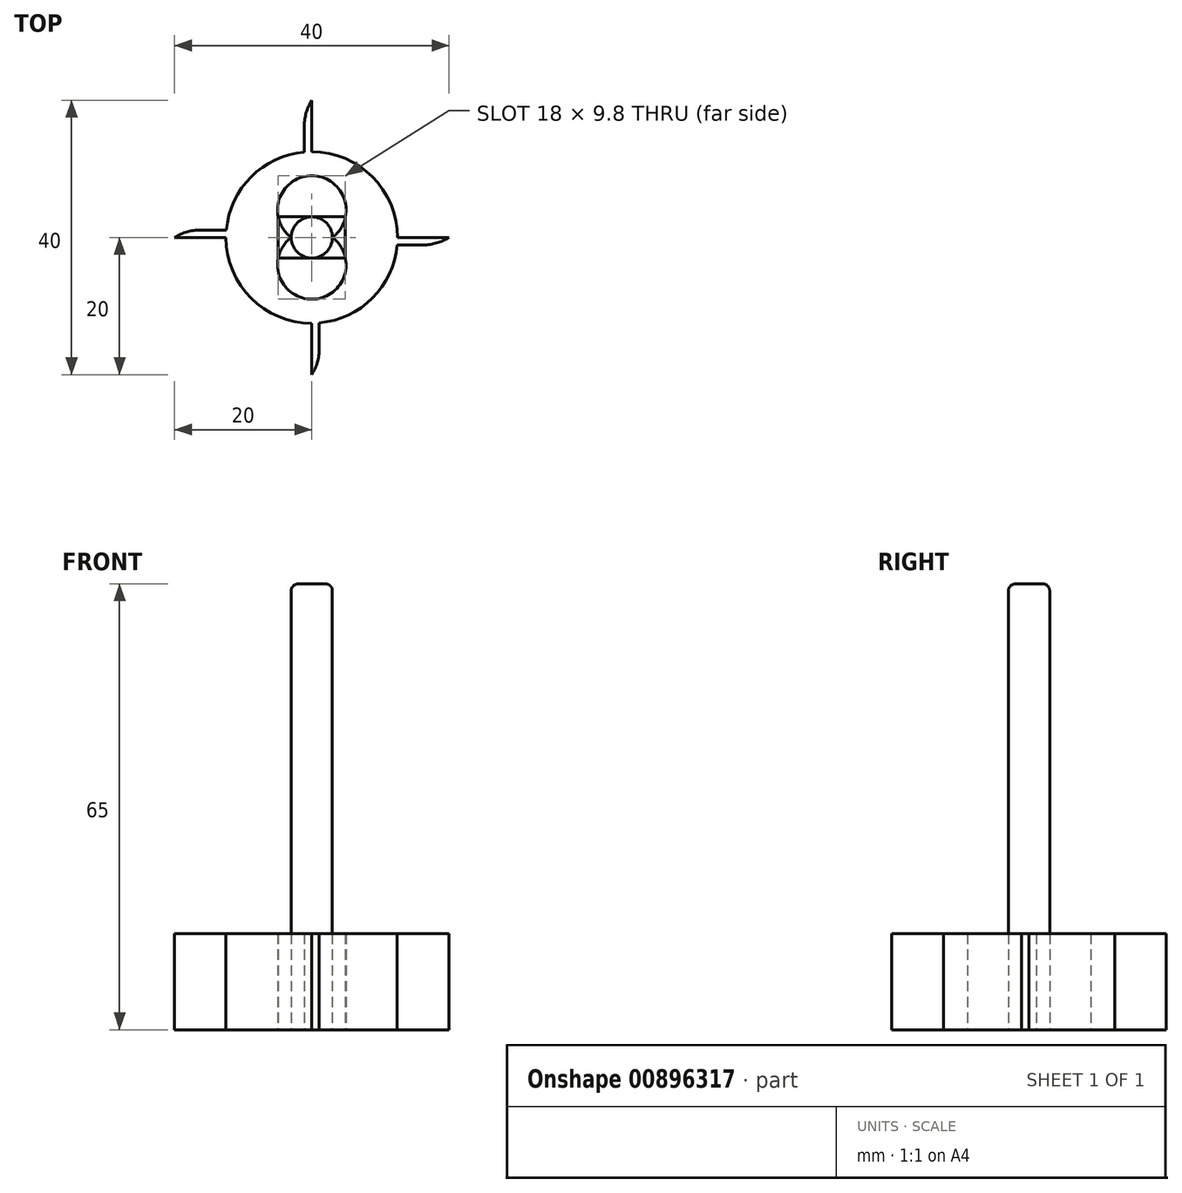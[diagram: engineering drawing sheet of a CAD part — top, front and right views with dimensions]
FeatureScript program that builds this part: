
annotation { "Feature Type Name" : "Feature", "Feature Type Description" : "" }
export const myFeature = defineFeature(function(context is Context, id is Id, definition is map)
    precondition{}
    {
        {
            var Q0;
            Q0=qCreatedBy(makeId("Top.planeOp"),FACE);
            var sketch = newSketch(context, id + "F0", { "sketchPlane" : qUnion([Q0])});
            skCircle(sketch, "E0", {"center": v(0, 0) * mm, "radius": 3 * mm});
            skCircle(sketch, "E1", {"center": v(0, 0) * mm, "radius": 12.5 * mm});
            skLineSegment(sketch, "E2", {"start": v(0, 0) * mm, "end": v(20, 0) * mm});
            skLineSegment(sketch, "E3", {"start": v(0, 0) * mm, "end": v(-20, 0) * mm});
            skArc(sketch, "E4", {"start": v(12.5, 0) * mm, "mid": v(16.25, -1.09) * mm, "end": v(20, 0) * mm});
            skLineSegment(sketch, "E5", {"start": v(0, 0) * mm, "end": v(0, -20) * mm});
            skLineSegment(sketch, "E6", {"start": v(0, -20) * mm, "end": v(0, 20) * mm});
            skLineSegment(sketch, "E7.MirrorCS", {"start": v(0, 20) * mm, "end": v(0, -20) * mm});
            skArc(sketch, "E8", {"start": v(0, -20) * mm, "mid": v(1.09, -16.25) * mm, "end": v(0, -12.5) * mm});
            skArc(sketch, "E9", {"start": v(-12.5, 0) * mm, "mid": v(-16.25, 1.09) * mm, "end": v(-20, 0) * mm});
            skArc(sketch, "E10", {"start": v(0, 20) * mm, "mid": v(-1.09, 16.25) * mm, "end": v(0, 12.5) * mm});
            skLineSegment(sketch, "E11", {"start": v(1.09, -16.25) * mm, "end": v(1.09, -12.45) * mm});
            skLineSegment(sketch, "E12", {"start": v(-16.25, 1.09) * mm, "end": v(-12.45, 1.09) * mm});
            skLineSegment(sketch, "E13", {"start": v(-1.09, 16.25) * mm, "end": v(-1.09, 12.45) * mm});
            skLineSegment(sketch, "E14", {"start": v(16.25, -1.09) * mm, "end": v(12.45, -1.09) * mm});
            skArc(sketch, "E15", {"start": v(-3, 0) * mm, "mid": v(0, -9) * mm, "end": v(3, 0) * mm});
            skArc(sketch, "E16", {"start": v(3, 0) * mm, "mid": v(0, 9) * mm, "end": v(-3, 0) * mm});
            skLineSegment(sketch, "E17", {"start": v(0, 3) * mm, "end": v(-4.9, 3) * mm});
            skLineSegment(sketch, "E18", {"start": v(-4.9, 3) * mm, "end": v(4.9, 3) * mm});
            skLineSegment(sketch, "E19", {"start": v(0, -3) * mm, "end": v(-4.9, -3) * mm});
            skLineSegment(sketch, "E20", {"start": v(-4.9, -3) * mm, "end": v(4.9, -3) * mm});
            skLineSegment(sketch, "E21", {"start": v(4.9, 3) * mm, "end": v(4.9, -3) * mm});
            skLineSegment(sketch, "E22", {"start": v(-4.9, 3) * mm, "end": v(-4.9, -3) * mm});
            skSolve(sketch);
        }
        {
            var Q0;
            {var subQ0=sQuery(id+"F0.wireOp",EDGE,"E5");var subQ1=sQuery(id+"F0.wireOp",EDGE,"E0");var subQ2=makeQuery(id+"F0.imprint","INTERSECT",VERTEX,{"derivedFrom":[subQ1,subQ0,sQuery(id+"F0.wireOp",EDGE,"E19"),sQuery(id+"F0.wireOp",EDGE,"E20")]});Q0=makeQuery(id+"F0.imprint","IMPRINT",FACE,{"disambiguationData":[TD([[makeQuery(id+"F0.imprint","IMPRINT",EDGE,{"disambiguationData":[TD([[subQ2,-1.0]])],"derivedFrom":subQ1}),1.0]])]});}
            var Q1;
            {var subQ0=sQuery(id+"F0.wireOp",EDGE,"E6");var subQ1=sQuery(id+"F0.wireOp",EDGE,"E0");var subQ2=makeQuery(id+"F0.imprint","INTERSECT",VERTEX,{"derivedFrom":[subQ1,subQ0,sQuery(id+"F0.wireOp",EDGE,"E17"),sQuery(id+"F0.wireOp",EDGE,"E18")]});Q1=makeQuery(id+"F0.imprint","IMPRINT",FACE,{"disambiguationData":[TD([[makeQuery(id+"F0.imprint","IMPRINT",EDGE,{"disambiguationData":[TD([[subQ2,1.0]])],"derivedFrom":subQ1}),1.0]])]});}
            var Q2;
            {var subQ0=sQuery(id+"F0.wireOp",EDGE,"E5");var subQ1=sQuery(id+"F0.wireOp",EDGE,"E0");var subQ2=makeQuery(id+"F0.imprint","INTERSECT",VERTEX,{"derivedFrom":[subQ1,subQ0,sQuery(id+"F0.wireOp",EDGE,"E19"),sQuery(id+"F0.wireOp",EDGE,"E20")]});var subQ7=sQuery(id+"F0.wireOp",EDGE,"E6");var subQ10=makeQuery(id+"F0.imprint","INTERSECT",VERTEX,{"derivedFrom":[subQ1,subQ7,sQuery(id+"F0.wireOp",EDGE,"E17"),sQuery(id+"F0.wireOp",EDGE,"E18")]});Q2=qUnion([makeQuery(id+"F0.imprint","IMPRINT",FACE,{"disambiguationData":[TD([[makeQuery(id+"F0.imprint","IMPRINT",EDGE,{"disambiguationData":[TD([[subQ10,-1.0]])],"derivedFrom":subQ1}),1.0]])]}),makeQuery(id+"F0.imprint","IMPRINT",FACE,{"disambiguationData":[TD([[makeQuery(id+"F0.imprint","IMPRINT",EDGE,{"disambiguationData":[TD([[subQ2,-1.0]])],"derivedFrom":subQ1}),1.0]])]})]);}
            var Q3;
            {var subQ0=sQuery(id+"F0.wireOp",EDGE,"E5");var subQ1=sQuery(id+"F0.wireOp",EDGE,"E0");var subQ2=makeQuery(id+"F0.imprint","INTERSECT",VERTEX,{"derivedFrom":[subQ1,subQ0,sQuery(id+"F0.wireOp",EDGE,"E19"),sQuery(id+"F0.wireOp",EDGE,"E20")]});Q3=makeQuery(id+"F0.imprint","IMPRINT",FACE,{"disambiguationData":[TD([[makeQuery(id+"F0.imprint","IMPRINT",EDGE,{"disambiguationData":[TD([[subQ2,1.0]])],"derivedFrom":subQ1}),1.0]])]});}
            extrude(context, id + "F1", {"entities" : qUnion([Q0, Q1, Q2, Q3]), "depth" : 65 * mm, "offsetDistance" : 25 * mm});
        }
        {
            var Q0;
            {var subQ1=sQuery(id+"F0.wireOp",EDGE,"E1");var subQ3=makeQuery(id+"F0.imprint","INTERSECT",VERTEX,{"derivedFrom":[subQ1,sQuery(id+"F0.wireOp",EDGE,"E12")]});Q0=makeQuery(id+"F0.imprint","IMPRINT",FACE,{"disambiguationData":[TD([[makeQuery(id+"F0.imprint","IMPRINT",EDGE,{"disambiguationData":[TD([[subQ3,1.0]])],"derivedFrom":subQ1}),1.0]])]});}
            var Q1;
            {var subQ0=sQuery(id+"F0.wireOp",EDGE,"E22");var subQ7=sQuery(id+"F0.wireOp",EDGE,"E3");var subQ8=makeQuery(id+"F0.imprint","INTERSECT",VERTEX,{"derivedFrom":[subQ7,subQ0]});Q1=makeQuery(id+"F0.imprint","IMPRINT",FACE,{"disambiguationData":[TD([[makeQuery(id+"F0.imprint","IMPRINT",EDGE,{"disambiguationData":[TD([[subQ8,-1.0]])],"derivedFrom":subQ7}),1.0]])]});}
            var Q2;
            {var subQ3=sQuery(id+"F0.wireOp",EDGE,"E1");var subQ6=makeQuery(id+"F0.imprint","INTERSECT",VERTEX,{"derivedFrom":[subQ3,sQuery(id+"F0.wireOp",EDGE,"E11")]});Q2=makeQuery(id+"F0.imprint","IMPRINT",FACE,{"disambiguationData":[TD([[makeQuery(id+"F0.imprint","IMPRINT",EDGE,{"disambiguationData":[TD([[subQ6,-1.0]])],"derivedFrom":subQ3}),1.0]])]});}
            var Q3;
            {var subQ5=sQuery(id+"F0.wireOp",EDGE,"E21");var subQ7=sQuery(id+"F0.wireOp",EDGE,"E2");var subQ8=makeQuery(id+"F0.imprint","INTERSECT",VERTEX,{"derivedFrom":[subQ7,subQ5]});Q3=makeQuery(id+"F0.imprint","IMPRINT",FACE,{"disambiguationData":[TD([[makeQuery(id+"F0.imprint","IMPRINT",EDGE,{"disambiguationData":[TD([[subQ8,-1.0]])],"derivedFrom":subQ7}),1.0]])]});}
            var Q4;
            {var subQ0=sQuery(id+"F0.wireOp",EDGE,"E17");Q4=makeQuery(id+"F0.imprint","IMPRINT",FACE,{"disambiguationData":[TD([[makeQuery(id+"F0.imprint","IMPRINT",EDGE,{"derivedFrom":subQ0}),1.0]])]});}
            var Q5;
            {var subQ0=sQuery(id+"F0.wireOp",EDGE,"E18");Q5=makeQuery(id+"F0.imprint","IMPRINT",FACE,{"disambiguationData":[TD([[makeQuery(id+"F0.imprint","IMPRINT",EDGE,{"derivedFrom":subQ0}),-1.0]])]});}
            var Q6;
            {var subQ0=sQuery(id+"F0.wireOp",EDGE,"E20");Q6=makeQuery(id+"F0.imprint","IMPRINT",FACE,{"disambiguationData":[TD([[makeQuery(id+"F0.imprint","IMPRINT",EDGE,{"derivedFrom":subQ0}),1.0]])]});}
            var Q7;
            {var subQ0=sQuery(id+"F0.wireOp",EDGE,"E19");Q7=makeQuery(id+"F0.imprint","IMPRINT",FACE,{"disambiguationData":[TD([[makeQuery(id+"F0.imprint","IMPRINT",EDGE,{"derivedFrom":subQ0}),-1.0]])]});}
            extrude(context, id + "F2", {"entities" : qUnion([Q0, Q1, Q2, Q3, Q4, Q5, Q6, Q7]), "operationType" : NewBodyOperationType.ADD, "depth" : 14 * mm, "offsetDistance" : 25 * mm});
        }
        {
            var Q0;
            {var subQ0=sQuery(id+"F0.wireOp",EDGE,"df6b5224-9f47-4030-86d7-f893336ae27f0.MirrorCS");Q0=makeQuery(id+"F0.imprint","IMPRINT",FACE,{"disambiguationData":[TD([[makeQuery(id+"F0.imprint","IMPRINT",EDGE,{"derivedFrom":subQ0}),1.0]])]});}
            var Q1;
            {var subQ0=sQuery(id+"F0.wireOp",EDGE,"E4");var subQ1=sQuery(id+"F0.wireOp",EDGE,"E2");var subQ3=makeQuery(id+"F0.imprint","INTERSECT",VERTEX,{"derivedFrom":[subQ1,subQ0]});Q1=makeQuery(id+"F0.imprint","IMPRINT",FACE,{"disambiguationData":[TD([[makeQuery(id+"F0.imprint","IMPRINT",EDGE,{"disambiguationData":[TD([[subQ3,1.0]])],"derivedFrom":subQ0}),1.0]])]});}
            var Q2;
            {var subQ0=sQuery(id+"F0.wireOp",EDGE,"HRuZR72R-Es62-5aXc-brnB-5MRJDPJZIia5");Q2=makeQuery(id+"F0.imprint","IMPRINT",FACE,{"disambiguationData":[TD([[makeQuery(id+"F0.imprint","IMPRINT",EDGE,{"derivedFrom":subQ0}),1.0]])]});}
            var Q3;
            {var subQ0=sQuery(id+"F0.wireOp",EDGE,"ade42b69-f09c-4982-8809-a60c7d5ba8530.MirrorCS");Q3=makeQuery(id+"F0.imprint","IMPRINT",FACE,{"disambiguationData":[TD([[makeQuery(id+"F0.imprint","IMPRINT",EDGE,{"derivedFrom":subQ0}),1.0]])]});}
            var Q4;
            {var subQ0=sQuery(id+"F0.wireOp",EDGE,"E10");var subQ1=sQuery(id+"F0.wireOp",EDGE,"E6");var subQ3=makeQuery(id+"F0.imprint","INTERSECT",VERTEX,{"derivedFrom":[subQ1,subQ0]});Q4=makeQuery(id+"F0.imprint","IMPRINT",FACE,{"disambiguationData":[TD([[makeQuery(id+"F0.imprint","IMPRINT",EDGE,{"disambiguationData":[TD([[subQ3,-1.0]])],"derivedFrom":subQ0}),1.0]])]});}
            var Q5;
            {var subQ0=sQuery(id+"F0.wireOp",EDGE,"E9");var subQ1=sQuery(id+"F0.wireOp",EDGE,"E3");var subQ3=makeQuery(id+"F0.imprint","INTERSECT",VERTEX,{"derivedFrom":[subQ1,subQ0]});Q5=makeQuery(id+"F0.imprint","IMPRINT",FACE,{"disambiguationData":[TD([[makeQuery(id+"F0.imprint","IMPRINT",EDGE,{"disambiguationData":[TD([[subQ3,1.0]])],"derivedFrom":subQ0}),1.0]])]});}
            var Q6;
            {var subQ0=sQuery(id+"F0.wireOp",EDGE,"E8");var subQ4=makeQuery(id+"F0.imprint","INTERSECT",VERTEX,{"derivedFrom":[subQ0,sQuery(id+"F0.wireOp",EDGE,"E11")]});Q6=makeQuery(id+"F0.imprint","IMPRINT",FACE,{"disambiguationData":[TD([[makeQuery(id+"F0.imprint","IMPRINT",EDGE,{"disambiguationData":[TD([[subQ4,1.0]])],"derivedFrom":subQ0}),1.0]])]});}
            var Q7;
            {var subQ3=sQuery(id+"F0.wireOp",EDGE,"E14");Q7=makeQuery(id+"F0.imprint","IMPRINT",FACE,{"disambiguationData":[TD([[makeQuery(id+"F0.imprint","IMPRINT",EDGE,{"derivedFrom":subQ3}),-1.0]])]});}
            var Q8;
            {var subQ3=sQuery(id+"F0.wireOp",EDGE,"E13");Q8=makeQuery(id+"F0.imprint","IMPRINT",FACE,{"disambiguationData":[TD([[makeQuery(id+"F0.imprint","IMPRINT",EDGE,{"derivedFrom":subQ3}),1.0]])]});}
            var Q9;
            {var subQ3=sQuery(id+"F0.wireOp",EDGE,"E12");Q9=makeQuery(id+"F0.imprint","IMPRINT",FACE,{"disambiguationData":[TD([[makeQuery(id+"F0.imprint","IMPRINT",EDGE,{"derivedFrom":subQ3}),-1.0]])]});}
            var Q10;
            {var subQ3=sQuery(id+"F0.wireOp",EDGE,"E11");Q10=makeQuery(id+"F0.imprint","IMPRINT",FACE,{"disambiguationData":[TD([[makeQuery(id+"F0.imprint","IMPRINT",EDGE,{"derivedFrom":subQ3}),1.0]])]});}
            extrude(context, id + "F3", {"entities" : qUnion([Q0, Q1, Q2, Q3, Q4, Q5, Q6, Q7, Q8, Q9, Q10]), "operationType" : NewBodyOperationType.ADD, "depth" : 14 * mm, "offsetDistance" : 25 * mm});
        }
        {
            var Q0;
            Q0=makeQuery(id+"F1.opExtrude","CAP_EDGE",EDGE,{"disambiguationData":[OSD([sQuery(id+"F0.wireOp",EDGE,"E0")])],"isStart":false});
            fillet(context, id + "F4", {"entities" : qUnion([Q0]), "radius" : 1 * mm, "tangentPropagation" : true, "allowEdgeOverflow" : false});
        }
        {
            var Q0;
            {var subQ0=sQuery(id+"F0.wireOp",EDGE,"E22");var subQ1=sQuery(id+"F0.wireOp",EDGE,"E3");var subQ2=makeQuery(id+"F0.imprint","INTERSECT",VERTEX,{"derivedFrom":[subQ1,subQ0]});Q0=makeQuery(id+"F0.imprint","IMPRINT",FACE,{"disambiguationData":[TD([[makeQuery(id+"F0.imprint","IMPRINT",EDGE,{"disambiguationData":[TD([[subQ2,-1.0]])],"derivedFrom":subQ0}),1.0]])]});}
            var Q1;
            {var subQ0=sQuery(id+"F0.wireOp",EDGE,"E22");var subQ1=sQuery(id+"F0.wireOp",EDGE,"E3");var subQ2=makeQuery(id+"F0.imprint","INTERSECT",VERTEX,{"derivedFrom":[subQ1,subQ0]});Q1=makeQuery(id+"F0.imprint","IMPRINT",FACE,{"disambiguationData":[TD([[makeQuery(id+"F0.imprint","IMPRINT",EDGE,{"disambiguationData":[TD([[subQ2,1.0]])],"derivedFrom":subQ0}),1.0]])]});}
            var Q2;
            {var subQ0=sQuery(id+"F0.wireOp",EDGE,"E21");var subQ1=sQuery(id+"F0.wireOp",EDGE,"E2");var subQ2=makeQuery(id+"F0.imprint","INTERSECT",VERTEX,{"derivedFrom":[subQ1,subQ0]});Q2=makeQuery(id+"F0.imprint","IMPRINT",FACE,{"disambiguationData":[TD([[makeQuery(id+"F0.imprint","IMPRINT",EDGE,{"disambiguationData":[TD([[subQ2,1.0]])],"derivedFrom":subQ0}),-1.0]])]});}
            var Q3;
            {var subQ0=sQuery(id+"F0.wireOp",EDGE,"E21");var subQ1=sQuery(id+"F0.wireOp",EDGE,"E2");var subQ2=makeQuery(id+"F0.imprint","INTERSECT",VERTEX,{"derivedFrom":[subQ1,subQ0]});Q3=makeQuery(id+"F0.imprint","IMPRINT",FACE,{"disambiguationData":[TD([[makeQuery(id+"F0.imprint","IMPRINT",EDGE,{"disambiguationData":[TD([[subQ2,-1.0]])],"derivedFrom":subQ0}),-1.0]])]});}
            extrude(context, id + "F5", {"entities" : qUnion([Q0, Q1, Q2, Q3]), "depth" : 14 * mm, "offsetDistance" : 25 * mm});
        }
    });
